# Revit family: 71_98_0501+0511_NESTED
name_source: partatom
category: Communication Devices
revit_build: Autodesk Revit 2015 (Build: 20141119_1515(x64)
units: mm (PartAtom-declared; Revit-internal decimal feet)

## types (6) — shared parameters
Basisplaat = Basisplaat
Breedte = 80 mm  [stored 0.262467 ft]
Consumption = 4 W
Default Elevation = 1219 mm
Diepte = 70 mm  [stored 0.229659 ft]
Dynamic range = > 90 dB
Frequency response = 200-20,000 Hz
Jack = Jack
Kabel = Kabel
Knoppen = Basisplaat
Lengte = 180 mm  [stored 0.590551 ft]
Load impedance = 8 Ω
Manufacturer = Televic Conference
Max output power = 1 W
Onderplaat = Inox
Scherm = Jack
Schroef = Basisplaat
Speaker = Jack
URL = http://www.televic-conference.com
Voltage = 48 V
Weight = 640

## per-type parameters (varying)
| type | Flexible microphone - 71.03.3540 | Microphone - 71.03.3140 | Model | Product ID | THD @ nominal level | Type 71.98.0511 | Type Comments |
| Type 71.98.0501 - flexible microphone | Yes | No | Confidea F-DD | 71.98.0501 | < 0.1% | No | Confidea Flushmount Delegate Discussion Unit |
| Type 71.98.0501 - microphone | No | Yes | Confidea F-DD | 71.98.0501 | < 0.1 % | No | Confidea Flushmount Delegate Discussion Unit |
| Type 71.98.0501 - no microphone | No | No | Confidea F-DD | 71.98.0551 | < 0.1 % | No | Confidea Flushmount Delegate Discussion Unit |
| Type 71.98.0511 - flexible microphone | Yes | No | Confidea F-CD | 71.98.0511 | < 0.1 % | Yes | Confidea Flushmount Chairman Discussion Unit |
| Type 71.98.0511 - microphone | No | Yes | Confidea F-CD | 71.98.0511 | < 0.1 % | Yes | Confidea Flushmount Chairman Discussion Unit |
| Type 71.98.0511 - no microphone | No | No | Confidea F-CD | 71.98.0511 | < 0.1 % | Yes | Confidea Flushmount Chairman Discussion Unit |

note: [stored X ft] marks values corroborated as IEEE doubles in the binary element streams (Revit-internal decimal feet)

## geometry (parser evidence)
native form markers: Sweep x12
no freeform markers — native parametric forms only
